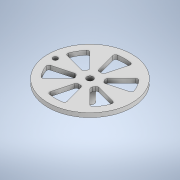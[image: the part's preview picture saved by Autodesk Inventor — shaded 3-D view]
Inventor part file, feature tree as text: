
AUTODESK INVENTOR PART (.ipt)
format: ipt  version: 2020 (Build 240168000, 168)  size: 225,792 bytes
history: native  units: in
note: dims shown in document units (in); Inventor stores cm internally (conversion verified against a paired STEP export)
features: extrude x5, sketch x5
ambient origin geometry x8: Origin, YZ Plane, XZ Plane, XY Plane, X Axis, Y Axis, Z Axis, Center Point
bodies: Solid1 (feature_tree)
feature tree (10):
  extrude  "Extrusion1"  Depth=0.5906in TaperAngle=0.0deg
  extrude  "Extrusion2"  Depth=0.5118in TaperAngle=0.0deg
  extrude  "Extrusion3"  Depth=0.1575in
  extrude  "Extrusion8"  Depth=3.1496in
  extrude  "Extrusion9"  TaperAngle=0.0deg  [1 undecoded]
  sketch  "Sketch1"  dims[d0=0.315in d1=0.5906in d2=0.0in]
  sketch  "Sketch2"  dims[d3=0.2362in d4=0.5118in d5=0.0in]
  sketch  "Sketch3"  dims[d8=0.1575in d9=0.1575in]
  sketch  "Sketch9"  dims[d10=0.9843in d11=0.0in d47=3.1496in]
  sketch  "Sketch10"  dims[d48=0.1575in d49=0.0in d50=0.0in d51=0.0in d54=0.1772in d58=15.0deg d60=30.0deg d61=0.7874in d62=0.0787in d63=0.0787in d64=2.3622in d66=360.0deg]
note: 1 required parameter value undecoded (feature->parameter linkage not recoverable at this tier; creation-order binding heuristic only, values carry confidence <= 0.55)
